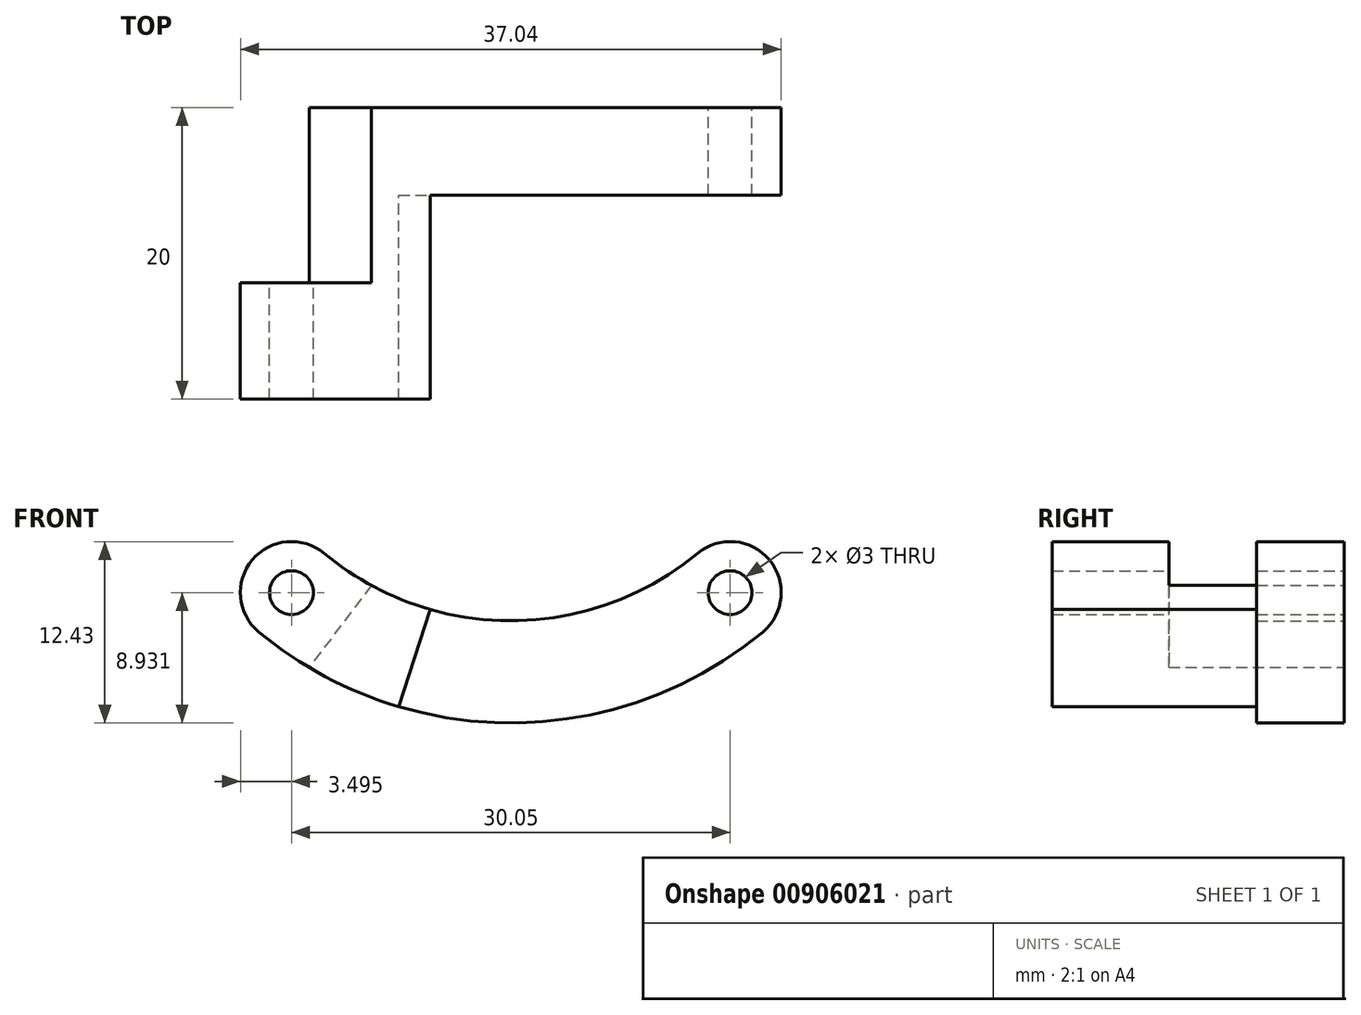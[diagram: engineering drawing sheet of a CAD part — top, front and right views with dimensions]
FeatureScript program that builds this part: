
annotation { "Feature Type Name" : "Feature", "Feature Type Description" : "" }
export const myFeature = defineFeature(function(context is Context, id is Id, definition is map)
    precondition{}
    {
        {
            var Q0;
            Q0=qCreatedBy(makeId("Front.planeOp"),FACE);
            var sketch = newSketch(context, id + "F0", { "sketchPlane" : qUnion([Q0])});
            skArc(sketch, "E0", {"start": v(-12.79, -15.38) * mm, "mid": v(0, -20) * mm, "end": v(12.79, -15.38) * mm});
            skArc(sketch, "E1", {"start": v(-17.26, -20.76) * mm, "mid": v(0, -27) * mm, "end": v(17.26, -20.76) * mm});
            skArc(sketch, "E2", {"start": v(-15.02, -18.07) * mm, "mid": v(0, -23.5) * mm, "end": v(15.03, -18.07) * mm});
            skArc(sketch, "E3", {"start": v(17.26, -20.76) * mm, "mid": v(17.72, -15.83) * mm, "end": v(12.79, -15.38) * mm});
            skArc(sketch, "E4", {"start": v(-12.79, -15.38) * mm, "mid": v(-17.72, -15.83) * mm, "end": v(-17.26, -20.76) * mm});
            skCircle(sketch, "E5", {"center": v(-15.02, -18.07) * mm, "radius": 1.5 * mm});
            skCircle(sketch, "E6", {"center": v(15.03, -18.07) * mm, "radius": 1.5 * mm});
            skSolve(sketch);
        }
        {
            var Q0;
            Q0=qSketchRegion(id+"F0",true);
            extrude(context, id + "F1", {"entities" : qUnion([Q0]), "endBound" : BoundingType.SYMMETRIC, "depth" : 20 * mm, "offsetDistance" : 25.4 * mm});
        }
        {
            var Q0;
            Q0=makeQuery(id+"F1.opExtrude","CAP_FACE",FACE,{"disambiguationData":[OSD([sQuery(id+"F0.wireOp",EDGE,"E0"),sQuery(id+"F0.wireOp",EDGE,"E1"),sQuery(id+"F0.wireOp",EDGE,"E3"),sQuery(id+"F0.wireOp",EDGE,"E4"),sQuery(id+"F0.wireOp",EDGE,"E5"),sQuery(id+"F0.wireOp",EDGE,"E6")])],"isStart":false});
            var sketch = newSketch(context, id + "F2", { "sketchPlane" : qUnion([Q0])});
            skLineSegment(sketch, "E7", {"start": v(-9.15, -30.5) * mm, "end": v(-2.4, -9.43) * mm});
            skLineSegment(sketch, "E8", {"start": v(-2.4, -9.43) * mm, "end": v(30.04, -11.8) * mm});
            skLineSegment(sketch, "E9", {"start": v(30.04, -11.8) * mm, "end": v(24.73, -32) * mm});
            skLineSegment(sketch, "E10", {"start": v(24.73, -32) * mm, "end": v(-9.15, -30.5) * mm});
            skSolve(sketch);
        }
        {
            var Q0;
            Q0=qSketchRegion(id+"F2",true);
            extrude(context, id + "F3", {"entities" : qUnion([Q0]), "operationType" : NewBodyOperationType.REMOVE, "oppositeDirection" : true, "depth" : 14 * mm, "offsetDistance" : 25.4 * mm});
        }
        {
            var Q0;
            Q0=makeQuery(id+"F1.opExtrude","CAP_FACE",FACE,{"disambiguationData":[OSD([sQuery(id+"F0.wireOp",EDGE,"E0"),sQuery(id+"F0.wireOp",EDGE,"E1"),sQuery(id+"F0.wireOp",EDGE,"E3"),sQuery(id+"F0.wireOp",EDGE,"E4"),sQuery(id+"F0.wireOp",EDGE,"E5"),sQuery(id+"F0.wireOp",EDGE,"E6")])],"isStart":true});
            var sketch = newSketch(context, id + "F4", { "sketchPlane" : qUnion([Q0])});
            skLineSegment(sketch, "E11", {"start": v(6.43, -13.47) * mm, "end": v(17.8, -28.46) * mm});
            skLineSegment(sketch, "E12", {"start": v(17.8, -28.46) * mm, "end": v(37.61, -8.65) * mm});
            skLineSegment(sketch, "E13", {"start": v(37.61, -8.65) * mm, "end": v(13.5, -6.4) * mm});
            skLineSegment(sketch, "E14", {"start": v(13.5, -6.4) * mm, "end": v(6.43, -13.47) * mm});
            skSolve(sketch);
        }
        {
            var Q0;
            Q0=qSketchRegion(id+"F4",true);
            extrude(context, id + "F5", {"entities" : qUnion([Q0]), "operationType" : NewBodyOperationType.REMOVE, "oppositeDirection" : true, "depth" : 12 * mm, "offsetDistance" : 25.4 * mm});
        }
    });
